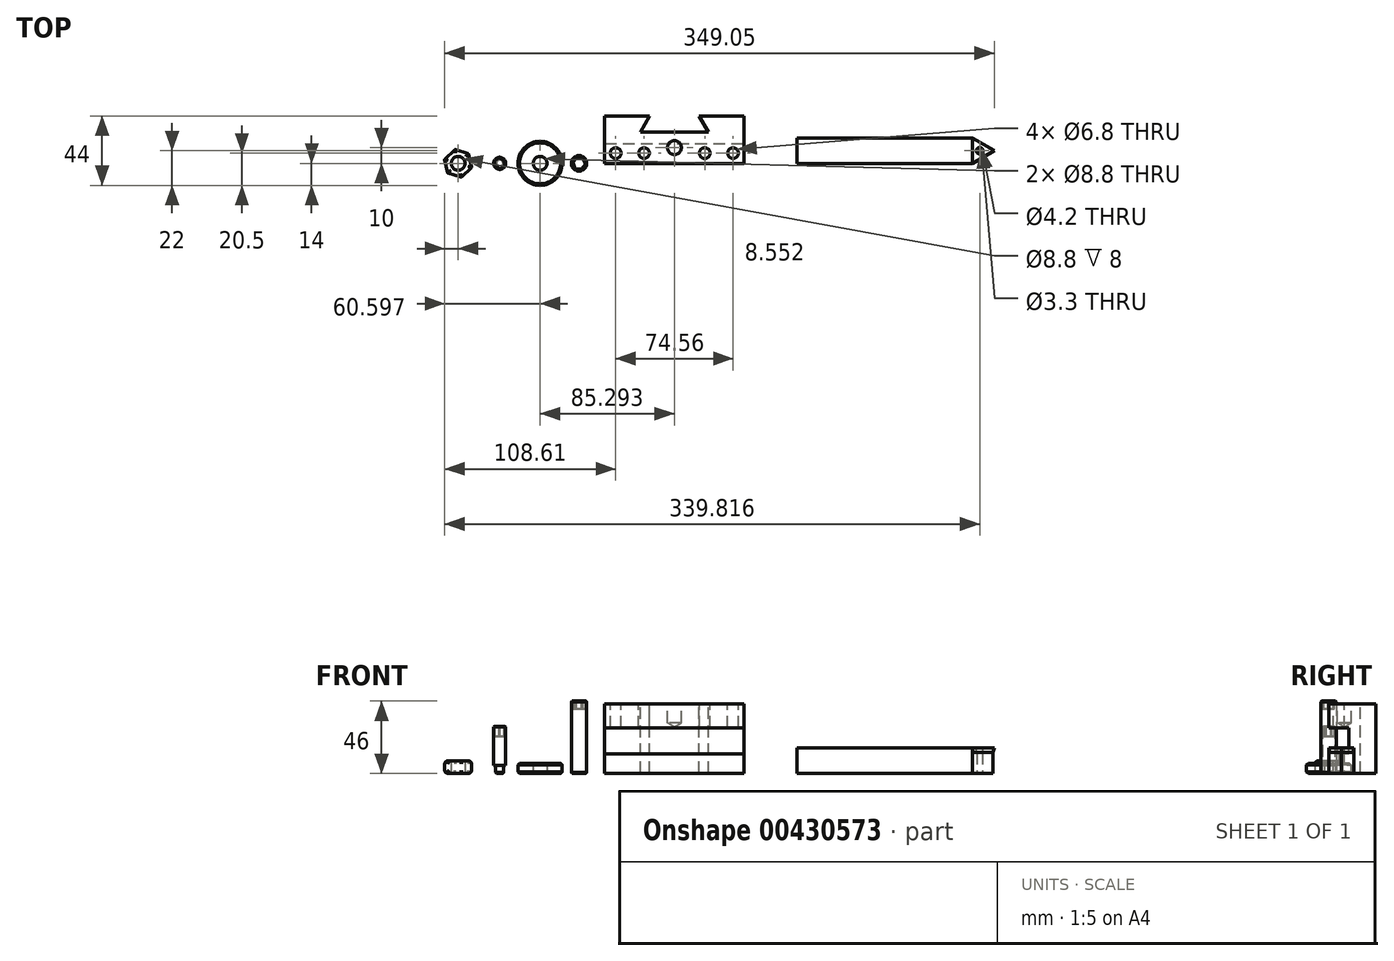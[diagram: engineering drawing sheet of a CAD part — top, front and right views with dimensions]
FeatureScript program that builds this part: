
annotation { "Feature Type Name" : "Feature", "Feature Type Description" : "" }
export const myFeature = defineFeature(function(context is Context, id is Id, definition is map)
    precondition{}
    {
        {
            var Q0;
            Q0=qCreatedBy(makeId("Front.planeOp"),FACE);
            var sketch = newSketch(context, id + "F0", { "sketchPlane" : qUnion([Q0])});
            skLineSegment(sketch, "E0.bottom", {"start": v(0, 0) * mm, "end": v(88.56, 0) * mm});
            skLineSegment(sketch, "E0.top", {"start": v(0, 44.12) * mm, "end": v(88.56, 44.12) * mm});
            skLineSegment(sketch, "E0.left", {"start": v(0, 0) * mm, "end": v(0, 44.12) * mm});
            skLineSegment(sketch, "E0.right", {"start": v(88.56, 0) * mm, "end": v(88.56, 44.12) * mm});
            skLineSegment(sketch, "E1", {"start": v(0, 12.4) * mm, "end": v(88.56, 12.4) * mm});
            skLineSegment(sketch, "E2", {"start": v(0, 28.9) * mm, "end": v(88.56, 28.9) * mm});
            skSolve(sketch);
        }
        {
            var Q0;
            Q0=qSketchRegion(id+"F0",true);
            extrude(context, id + "F1", {"entities" : qUnion([Q0]), "oppositeDirection" : true, "depth" : 30 * mm});
        }
        {
            var Q0;
            {var subQ0=sQuery(id+"F0.wireOp",EDGE,"E1");Q0=makeQuery(id+"F0.imprint","IMPRINT",FACE,{"disambiguationData":[TD([[makeQuery(id+"F0.imprint","IMPRINT",EDGE,{"derivedFrom":subQ0}),1.0]])]});}
            extrude(context, id + "F2", {"entities" : qUnion([Q0]), "operationType" : NewBodyOperationType.REMOVE, "oppositeDirection" : true, "depth" : 12.7 * mm});
        }
        {
            var Q0;
            Q0=makeQuery(id+"F1.opExtrude","SWEPT_FACE",FACE,{"disambiguationData":[OSD([sQuery(id+"F0.wireOp",EDGE,"E0.top")])]});
            var sketch = newSketch(context, id + "F3", { "sketchPlane" : qUnion([Q0])});
            skLineSegment(sketch, "E3", {"start": v(0, 6.5) * mm, "end": v(88.56, 6.5) * mm, "construction": true});
            skPoint(sketch, "E4", {"position": v(7, 6.5) * mm});
            skPoint(sketch, "E5", {"position": v(25, 6.5) * mm});
            skPoint(sketch, "E6", {"position": v(81.56, 6.5) * mm});
            skPoint(sketch, "E7", {"position": v(63.56, 6.5) * mm});
            skLineSegment(sketch, "E8", {"start": v(22.78, 20) * mm, "end": v(65.78, 20) * mm});
            skLineSegment(sketch, "E9", {"start": v(44.28, 17.17) * mm, "end": v(44.28, 26.13) * mm, "construction": true});
            skPoint(sketch, "E9.startSnap0", {"position": v(44.28, 30) * mm});
            skLineSegment(sketch, "E10", {"start": v(65.78, 20) * mm, "end": v(60, 30) * mm});
            skLineSegment(sketch, "E11", {"start": v(22.78, 20) * mm, "end": v(28.55, 30) * mm});
            skLineSegment(sketch, "E12", {"start": v(36.04, 10) * mm, "end": v(51.79, 10) * mm, "construction": true});
            skPoint(sketch, "E13", {"position": v(44.28, 10) * mm});
            skSolve(sketch);
        }
        {
            var Q0;
            Q0=qSketchRegion(id+"F3",true);
            var Q1;
            Q1=makeQuery(id+"F3.imprint","IMPRINT",FACE,{"disambiguationData":[TD([[makeQuery(id+"F3.imprint","IMPRINT",EDGE,{"derivedFrom":sQuery(id+"F3.wireOp",EDGE,"E8")}),1.0]])]});
            extrude(context, id + "F4", {"entities" : qUnion([Q0, Q1]), "operationType" : NewBodyOperationType.REMOVE, "endBound" : BoundingType.UP_TO_NEXT, "oppositeDirection" : true, "depth" : 25 * mm});
        }
        {
            var Q0;
            Q0=sQuery(id+"F3.wireOp",VERTEX,"E4");
            var Q1;
            Q1=sQuery(id+"F3.wireOp",VERTEX,"E5");
            var Q2;
            Q2=sQuery(id+"F3.wireOp",VERTEX,"E7");
            var Q3;
            Q3=sQuery(id+"F3.wireOp",VERTEX,"E6");
            var Q4;
            Q4=makeQuery(id+"F1.opExtrude","SWEPT_BODY",BODY,{"disambiguationData":[OSD([sQuery(id+"F0.wireOp",EDGE,"E0.bottom"),sQuery(id+"F0.wireOp",EDGE,"E0.top"),sQuery(id+"F0.wireOp",EDGE,"E0.left"),sQuery(id+"F0.wireOp",EDGE,"E0.right")])]});
            hole(context, id + "F5", {"style" : HoleStyle.SIMPLE, "endStyle" : HoleEndStyle.BLIND, "standardTappedOrClearance" : lookupTablePath({ "standard" : "ISO", "engagement" : "75%", "pitch" : "1.25 mm", "size" : "M8", "type" : "Tapped" }), "standardBlindInLast" : lookupTablePath({ "standard" : "ISO", "engagement" : "75%", "pitch" : "1.25 mm", "size" : "M8", "type" : "Tapped" }), "holeDiameter" : 6.8 * mm, "showTappedDepth" : true, "holeDepth" : 15.75 * mm, "isTappedThrough" : true, "tappedDepth" : 12 * mm, "tapClearance" : 3, "startFromSketch" : true, "locations" : qUnion([Q0, Q1, Q2, Q3]), "scope" : qUnion([Q4]), "majorDiameter" : 8 * mm});
        }
        {
            var Q0;
            Q0=sQuery(id+"F3.wireOp",VERTEX,"E13");
            var Q1;
            Q1=makeQuery(id+"F1.opExtrude","SWEPT_BODY",BODY,{"disambiguationData":[OSD([sQuery(id+"F0.wireOp",EDGE,"E0.bottom"),sQuery(id+"F0.wireOp",EDGE,"E0.top"),sQuery(id+"F0.wireOp",EDGE,"E0.left"),sQuery(id+"F0.wireOp",EDGE,"E0.right")])]});
            hole(context, id + "F6", {"style" : HoleStyle.SIMPLE, "endStyle" : HoleEndStyle.BLIND, "standardTappedOrClearance" : lookupTablePath({ "standard" : "ISO", "engagement" : "75%", "pitch" : "1.25 mm", "size" : "M10", "type" : "Tapped" }), "standardBlindInLast" : lookupTablePath({ "standard" : "ISO", "engagement" : "75%", "pitch" : "1.25 mm", "size" : "M10", "type" : "Tapped" }), "holeDiameter" : 8.8 * mm, "showTappedDepth" : true, "holeDepth" : 12 * mm, "isTappedThrough" : true, "tappedDepth" : 8.25 * mm, "tapClearance" : 3, "startFromSketch" : true, "locations" : qUnion([Q0]), "scope" : qUnion([Q1]), "majorDiameter" : 10 * mm});
        }
        {
            var Q0;
            Q0=qCreatedBy(makeId("Top.planeOp"),FACE);
            var sketch = newSketch(context, id + "F7", { "sketchPlane" : qUnion([Q0])});
            skCircle(sketch, "E14", {"center": v(-16.29, 0) * mm, "radius": 4.9 * mm});
            skSolve(sketch);
        }
        {
            var Q0;
            Q0=qSketchRegion(id+"F7",true);
            extrude(context, id + "F8", {"entities" : qUnion([Q0]), "depth" : 46 * mm});
        }
        {
            var Q0;
            Q0=makeQuery(id+"F8.opExtrude","CAP_EDGE",EDGE,{"disambiguationData":[OSD([sQuery(id+"F7.wireOp",EDGE,"E14")])],"isStart":false});
            var Q1;
            Q1=makeQuery(id+"F8.opExtrude","CAP_EDGE",EDGE,{"disambiguationData":[OSD([sQuery(id+"F7.wireOp",EDGE,"E14")])],"isStart":true});
            chamfer(context, id + "F9", {"entities" : qUnion([Q0, Q1]), "width" : .5 * mm, "tangentPropagation" : true});
        }
        {
            var Q0;
            Q0=makeQuery(id+"F8.opExtrude","CAP_FACE",FACE,{"disambiguationData":[OSD([sQuery(id+"F7.wireOp",EDGE,"E14")])],"isStart":false});
            var sketch = newSketch(context, id + "F10", { "sketchPlane" : qUnion([Q0])});
            skCircle(sketch, "E15.cCircle", {"center": v(-16.29, 0) * mm, "radius": 4 * mm, "construction": true});
            skLineSegment(sketch, "E15.0", {"start": v(-13.87, 3.19) * mm, "end": v(-12.32, -0.5) * mm});
            skLineSegment(sketch, "E15.1", {"start": v(-12.32, -0.5) * mm, "end": v(-14.73, -3.69) * mm});
            skLineSegment(sketch, "E15.2", {"start": v(-14.73, -3.69) * mm, "end": v(-18.7, -3.19) * mm});
            skLineSegment(sketch, "E15.3", {"start": v(-18.7, -3.19) * mm, "end": v(-20.26, 0.5) * mm});
            skLineSegment(sketch, "E15.4", {"start": v(-20.26, 0.5) * mm, "end": v(-17.84, 3.69) * mm});
            skLineSegment(sketch, "E15.5", {"start": v(-17.84, 3.69) * mm, "end": v(-13.87, 3.19) * mm});
            skSolve(sketch);
        }
        {
            var Q0;
            Q0=makeQuery(id+"F10.imprint","IMPRINT",FACE,{"disambiguationData":[TD([[makeQuery(id+"F10.imprint","IMPRINT",EDGE,{"derivedFrom":sQuery(id+"F10.wireOp",EDGE,"E15.0")}),-1.0]])]});
            extrude(context, id + "F11", {"entities" : qUnion([Q0]), "operationType" : NewBodyOperationType.REMOVE, "oppositeDirection" : true, "depth" : 5 * mm});
        }
        {
            var Q0;
            Q0=qCreatedBy(makeId("Top.planeOp"),FACE);
            var sketch = newSketch(context, id + "F12", { "sketchPlane" : qUnion([Q0])});
            skCircle(sketch, "E16", {"center": v(-41.01, 0) * mm, "radius": 14 * mm});
            skSolve(sketch);
        }
        {
            var Q0;
            Q0=makeQuery(id+"F12.imprint","IMPRINT",FACE,{"disambiguationData":[TD([[makeQuery(id+"F12.imprint","IMPRINT",EDGE,{"derivedFrom":sQuery(id+"F12.wireOp",EDGE,"E16")}),1.0]])]});
            extrude(context, id + "F13", {"entities" : qUnion([Q0]), "depth" : 6.43 * mm});
        }
        {
            var Q0;
            Q0=makeQuery(id+"F13.opExtrude","CAP_EDGE",EDGE,{"disambiguationData":[OSD([sQuery(id+"F12.wireOp",EDGE,"E16")])],"isStart":false});
            var Q1;
            Q1=makeQuery(id+"F13.opExtrude","CAP_EDGE",EDGE,{"disambiguationData":[OSD([sQuery(id+"F12.wireOp",EDGE,"E16")])],"isStart":true});
            chamfer(context, id + "F14", {"entities" : qUnion([Q0, Q1]), "width" : 1 * mm, "tangentPropagation" : true});
        }
        {
            var Q0;
            Q0=sQuery(id+"F12.wireOp",VERTEX,"E16.center");
            var Q1;
            Q1=makeQuery(id+"F13.opExtrude","SWEPT_BODY",BODY,{"disambiguationData":[OSD([sQuery(id+"F12.wireOp",EDGE,"E16")])]});
            hole(context, id + "F15", {"style" : HoleStyle.SIMPLE, "endStyle" : HoleEndStyle.THROUGH, "oppositeDirection" : true, "standardTappedOrClearance" : lookupTablePath({ "standard" : "ISO", "engagement" : "75%", "pitch" : "1.25 mm", "size" : "M10", "type" : "Tapped" }), "standardBlindInLast" : lookupTablePath({ "standard" : "ISO", "engagement" : "75%", "pitch" : "1.25 mm", "size" : "M10", "type" : "Tapped" }), "holeDiameter" : 8.8 * mm, "showTappedDepth" : true, "isTappedThrough" : true, "tappedDepth" : 12 * mm, "tapClearance" : 3, "startFromSketch" : true, "locations" : qUnion([Q0]), "scope" : qUnion([Q1]), "majorDiameter" : 10 * mm});
        }
        {
            var Q0;
            Q0=qCreatedBy(makeId("Top.planeOp"),FACE);
            var sketch = newSketch(context, id + "F16", { "sketchPlane" : qUnion([Q0])});
            skCircle(sketch, "E17", {"center": v(-66.7, 0) * mm, "radius": 2.6 * mm});
            skSolve(sketch);
        }
        {
            var Q0;
            Q0=qSketchRegion(id+"F16",true);
            extrude(context, id + "F17", {"entities" : qUnion([Q0]), "depth" : 5 * mm});
        }
        {
            var Q0;
            Q0=makeQuery(id+"F17.opExtrude","CAP_FACE",FACE,{"disambiguationData":[OSD([sQuery(id+"F16.wireOp",EDGE,"E17")])],"isStart":false});
            var sketch = newSketch(context, id + "F18", { "sketchPlane" : qUnion([Q0])});
            skCircle(sketch, "E18", {"center": v(-66.7, 0) * mm, "radius": 3.85 * mm});
            skSolve(sketch);
        }
        {
            var Q0;
            Q0=qSketchRegion(id+"F18",true);
            extrude(context, id + "F19", {"entities" : qUnion([Q0]), "operationType" : NewBodyOperationType.ADD, "depth" : 25 * mm});
        }
        {
            var Q0;
            Q0=makeQuery(id+"F19.opExtrude","CAP_FACE",FACE,{"disambiguationData":[OSD([sQuery(id+"F18.wireOp",EDGE,"E18")])],"isStart":false});
            var sketch = newSketch(context, id + "F20", { "sketchPlane" : qUnion([Q0])});
            skCircle(sketch, "E19.cCircle", {"center": v(-66.7, 0) * mm, "radius": 3.03 * mm, "construction": true});
            skLineSegment(sketch, "E19.0", {"start": v(-67, 3.49) * mm, "end": v(-63.82, 2) * mm});
            skLineSegment(sketch, "E19.1", {"start": v(-63.82, 2) * mm, "end": v(-63.52, -1.48) * mm});
            skLineSegment(sketch, "E19.2", {"start": v(-63.52, -1.48) * mm, "end": v(-66.39, -3.49) * mm});
            skLineSegment(sketch, "E19.3", {"start": v(-66.39, -3.49) * mm, "end": v(-69.56, -2) * mm});
            skLineSegment(sketch, "E19.4", {"start": v(-69.56, -2) * mm, "end": v(-69.86, 1.48) * mm});
            skLineSegment(sketch, "E19.5", {"start": v(-69.86, 1.48) * mm, "end": v(-67, 3.49) * mm});
            skPoint(sketch, "E19.0.midPoint", {"position": v(-65.41, 2.75) * mm});
            skSolve(sketch);
        }
        {
            var Q0;
            Q0=makeQuery(id+"F20.imprint","IMPRINT",FACE,{"disambiguationData":[TD([[makeQuery(id+"F20.imprint","IMPRINT",EDGE,{"derivedFrom":sQuery(id+"F20.wireOp",EDGE,"E19.0")}),-1.0]])]});
            extrude(context, id + "F21", {"entities" : qUnion([Q0]), "operationType" : NewBodyOperationType.REMOVE, "oppositeDirection" : true, "depth" : 6.4 * mm});
        }
        {
            var Q0;
            Q0=qCreatedBy(makeId("Top.planeOp"),FACE);
            var sketch = newSketch(context, id + "F22", { "sketchPlane" : qUnion([Q0])});
            skCircle(sketch, "E20.cCircle", {"center": v(-93.06, 0) * mm, "radius": 9 * mm, "construction": true});
            skLineSegment(sketch, "E20.0", {"start": v(-86.48, 6.14) * mm, "end": v(-84.45, -2.63) * mm});
            skLineSegment(sketch, "E20.1", {"start": v(-84.45, -2.63) * mm, "end": v(-91.03, -8.77) * mm});
            skLineSegment(sketch, "E20.2", {"start": v(-91.03, -8.77) * mm, "end": v(-99.64, -6.14) * mm});
            skLineSegment(sketch, "E20.3", {"start": v(-99.64, -6.14) * mm, "end": v(-101.67, 2.63) * mm});
            skLineSegment(sketch, "E20.4", {"start": v(-101.67, 2.63) * mm, "end": v(-95.09, 8.77) * mm});
            skLineSegment(sketch, "E20.5", {"start": v(-95.09, 8.77) * mm, "end": v(-86.48, 6.14) * mm});
            skSolve(sketch);
        }
        {
            var Q0;
            Q0=makeQuery(id+"F22.imprint","IMPRINT",FACE,{"disambiguationData":[TD([[makeQuery(id+"F22.imprint","IMPRINT",EDGE,{"derivedFrom":sQuery(id+"F22.wireOp",EDGE,"E20.0")}),-1.0]])]});
            extrude(context, id + "F23", {"entities" : qUnion([Q0]), "depth" : 8 * mm});
        }
        {
            var Q0;
            Q0=sQuery(id+"F22.wireOp",VERTEX,"E20.cCircle.center");
            var Q1;
            Q1=makeQuery(id+"F23.opExtrude","SWEPT_BODY",BODY,{"disambiguationData":[OSD([sQuery(id+"F22.wireOp",EDGE,"E20.0"),sQuery(id+"F22.wireOp",EDGE,"E20.1"),sQuery(id+"F22.wireOp",EDGE,"E20.2"),sQuery(id+"F22.wireOp",EDGE,"E20.3"),sQuery(id+"F22.wireOp",EDGE,"E20.4"),sQuery(id+"F22.wireOp",EDGE,"E20.5")])]});
            hole(context, id + "F24", {"style" : HoleStyle.SIMPLE, "endStyle" : HoleEndStyle.THROUGH, "oppositeDirection" : true, "standardTappedOrClearance" : lookupTablePath({ "standard" : "ISO", "engagement" : "75%", "pitch" : "1.25 mm", "size" : "M10", "type" : "Tapped" }), "standardBlindInLast" : lookupTablePath({ "standard" : "ISO", "engagement" : "75%", "pitch" : "1.25 mm", "size" : "M10", "type" : "Tapped" }), "holeDiameter" : 8.8 * mm, "showTappedDepth" : true, "isTappedThrough" : true, "tappedDepth" : 12 * mm, "tapClearance" : 3, "startFromSketch" : true, "locations" : qUnion([Q0]), "scope" : qUnion([Q1]), "majorDiameter" : 10 * mm});
        }
        {
            var Q0;
            Q0=makeQuery(id+"F23.opExtrude","CAP_EDGE",EDGE,{"disambiguationData":[OSD([sQuery(id+"F22.wireOp",EDGE,"E20.4")])],"isStart":false});
            var Q1;
            Q1=makeQuery(id+"F23.opExtrude","CAP_EDGE",EDGE,{"disambiguationData":[OSD([sQuery(id+"F22.wireOp",EDGE,"E20.5")])],"isStart":false});
            var Q2;
            Q2=makeQuery(id+"F23.opExtrude","CAP_EDGE",EDGE,{"disambiguationData":[OSD([sQuery(id+"F22.wireOp",EDGE,"E20.0")])],"isStart":false});
            var Q3;
            Q3=makeQuery(id+"F23.opExtrude","CAP_EDGE",EDGE,{"disambiguationData":[OSD([sQuery(id+"F22.wireOp",EDGE,"E20.1")])],"isStart":false});
            var Q4;
            Q4=makeQuery(id+"F23.opExtrude","CAP_EDGE",EDGE,{"disambiguationData":[OSD([sQuery(id+"F22.wireOp",EDGE,"E20.2")])],"isStart":false});
            var Q5;
            Q5=makeQuery(id+"F23.opExtrude","CAP_EDGE",EDGE,{"disambiguationData":[OSD([sQuery(id+"F22.wireOp",EDGE,"E20.3")])],"isStart":false});
            var Q6;
            Q6=makeQuery(id+"F23.opExtrude","CAP_EDGE",EDGE,{"disambiguationData":[OSD([sQuery(id+"F22.wireOp",EDGE,"E20.3")])],"isStart":true});
            var Q7;
            Q7=makeQuery(id+"F23.opExtrude","CAP_EDGE",EDGE,{"disambiguationData":[OSD([sQuery(id+"F22.wireOp",EDGE,"E20.4")])],"isStart":true});
            var Q8;
            Q8=makeQuery(id+"F23.opExtrude","CAP_EDGE",EDGE,{"disambiguationData":[OSD([sQuery(id+"F22.wireOp",EDGE,"E20.5")])],"isStart":true});
            var Q9;
            Q9=makeQuery(id+"F23.opExtrude","CAP_EDGE",EDGE,{"disambiguationData":[OSD([sQuery(id+"F22.wireOp",EDGE,"E20.0")])],"isStart":true});
            var Q10;
            Q10=makeQuery(id+"F23.opExtrude","CAP_EDGE",EDGE,{"disambiguationData":[OSD([sQuery(id+"F22.wireOp",EDGE,"E20.1")])],"isStart":true});
            var Q11;
            Q11=makeQuery(id+"F23.opExtrude","CAP_EDGE",EDGE,{"disambiguationData":[OSD([sQuery(id+"F22.wireOp",EDGE,"E20.2")])],"isStart":true});
            fillet(context, id + "F25", {"entities" : qUnion([Q0, Q1, Q2, Q3, Q4, Q5, Q6, Q7, Q8, Q9, Q10, Q11]), "radius" : 2 * mm, "tangentPropagation" : true, "allowEdgeOverflow" : false});
        }
        {
            var Q0;
            Q0=makeQuery(id+"F23.opExtrude","SWEPT_EDGE",EDGE,{"disambiguationData":[OSD([sQuery(id+"F22.wireOp",EDGE,"E20.2"),sQuery(id+"F22.wireOp",EDGE,"E20.3")])]});
            var Q1;
            Q1=makeQuery(id+"F23.opExtrude","SWEPT_EDGE",EDGE,{"disambiguationData":[OSD([sQuery(id+"F22.wireOp",EDGE,"E20.1"),sQuery(id+"F22.wireOp",EDGE,"E20.2")])]});
            var Q2;
            Q2=makeQuery(id+"F23.opExtrude","SWEPT_EDGE",EDGE,{"disambiguationData":[OSD([sQuery(id+"F22.wireOp",EDGE,"E20.0"),sQuery(id+"F22.wireOp",EDGE,"E20.1")])]});
            var Q3;
            Q3=makeQuery(id+"F23.opExtrude","SWEPT_EDGE",EDGE,{"disambiguationData":[OSD([sQuery(id+"F22.wireOp",EDGE,"E20.3"),sQuery(id+"F22.wireOp",EDGE,"E20.4")])]});
            var Q4;
            Q4=makeQuery(id+"F23.opExtrude","SWEPT_EDGE",EDGE,{"disambiguationData":[OSD([sQuery(id+"F22.wireOp",EDGE,"E20.4"),sQuery(id+"F22.wireOp",EDGE,"E20.5")])]});
            var Q5;
            Q5=makeQuery(id+"F23.opExtrude","SWEPT_EDGE",EDGE,{"disambiguationData":[OSD([sQuery(id+"F22.wireOp",EDGE,"E20.0"),sQuery(id+"F22.wireOp",EDGE,"E20.5")])]});
            fillet(context, id + "F26", {"entities" : qUnion([Q0, Q1, Q2, Q3, Q4, Q5]), "radius" : .5 * mm, "tangentPropagation" : true, "allowEdgeOverflow" : false});
        }
        {
            var Q0;
            Q0=qCreatedBy(makeId("Front.planeOp"),FACE);
            var sketch = newSketch(context, id + "F27", { "sketchPlane" : qUnion([Q0])});
            skLineSegment(sketch, "E21.bottom", {"start": v(122.09, 0) * mm, "end": v(245.45, 0) * mm});
            skLineSegment(sketch, "E21.top", {"start": v(122.09, 16.3) * mm, "end": v(233.59, 16.3) * mm});
            skLineSegment(sketch, "E21.left", {"start": v(122.09, 0) * mm, "end": v(122.09, 16.3) * mm});
            skLineSegment(sketch, "E22", {"start": v(233.59, 16.3) * mm, "end": v(233.59, 13.3) * mm});
            skLineSegment(sketch, "E23", {"start": v(233.59, 13.3) * mm, "end": v(246.59, 13.3) * mm});
            skLineSegment(sketch, "E24", {"start": v(246.59, 13.3) * mm, "end": v(246.59, 0) * mm});
            skLineSegment(sketch, "E25", {"start": v(246.59, 0) * mm, "end": v(245.45, 0) * mm});
            skSolve(sketch);
        }
        {
            var Q0;
            Q0=makeQuery(id+"F27.imprint","IMPRINT",FACE,{"disambiguationData":[TD([[makeQuery(id+"F27.imprint","IMPRINT",EDGE,{"derivedFrom":sQuery(id+"F27.wireOp",EDGE,"E21.bottom")}),1.0]])]});
            extrude(context, id + "F28", {"entities" : qUnion([Q0]), "oppositeDirection" : true, "depth" : 16 * mm});
        }
        {
            var Q0;
            Q0=makeQuery(id+"F28.opExtrude","SWEPT_FACE",FACE,{"disambiguationData":[OSD([sQuery(id+"F27.wireOp",EDGE,"E23")])]});
            var sketch = newSketch(context, id + "F29", { "sketchPlane" : qUnion([Q0])});
            skLineSegment(sketch, "E26", {"start": v(233.59, 16) * mm, "end": v(246.59, 8) * mm});
            skLineSegment(sketch, "E27", {"start": v(246.59, 8) * mm, "end": v(233.59, 0) * mm});
            skSolve(sketch);
        }
        {
            var Q0;
            {var subQ0=sQuery(id+"F29.wireOp",EDGE,"E26");Q0=makeQuery(id+"F29.imprint","IMPRINT",FACE,{"disambiguationData":[TD([[makeQuery(id+"F29.imprint","IMPRINT",EDGE,{"derivedFrom":subQ0}),1.0]])]});}
            var Q1;
            {var subQ0=sQuery(id+"F29.wireOp",EDGE,"E27");Q1=makeQuery(id+"F29.imprint","IMPRINT",FACE,{"disambiguationData":[TD([[makeQuery(id+"F29.imprint","IMPRINT",EDGE,{"derivedFrom":subQ0}),1.0]])]});}
            extrude(context, id + "F30", {"entities" : qUnion([Q0, Q1]), "operationType" : NewBodyOperationType.REMOVE, "endBound" : BoundingType.UP_TO_NEXT, "oppositeDirection" : true, "depth" : 25 * mm});
        }
        {
            var Q0;
            Q0=makeQuery(id+"F28.opExtrude","SWEPT_FACE",FACE,{"disambiguationData":[OSD([sQuery(id+"F27.wireOp",EDGE,"E21.top")])]});
            var sketch = newSketch(context, id + "F31", { "sketchPlane" : qUnion([Q0])});
            skLineSegment(sketch, "E28", {"start": v(233.59, 0) * mm, "end": v(247.44, 8) * mm});
            skLineSegment(sketch, "E29", {"start": v(247.44, 8) * mm, "end": v(233.59, 16) * mm});
            skLineSegment(sketch, "E30", {"start": v(233.59, 16) * mm, "end": v(233.59, 0) * mm});
            skLineSegment(sketch, "E31", {"start": v(247.44, 8) * mm, "end": v(233.59, 8) * mm, "construction": true});
            skLineSegment(sketch, "E32", {"start": v(233.59, 0) * mm, "end": v(240.52, 12) * mm, "construction": true});
            skPoint(sketch, "E33", {"position": v(238.2, 8) * mm});
            skSolve(sketch);
        }
        {
            var Q0;
            Q0=qSketchRegion(id+"F31",true);
            extrude(context, id + "F32", {"entities" : qUnion([Q0]), "oppositeDirection" : true, "depth" : 3 * mm, "hasDraft" : true, "draftAngle" : 7 * degree, "draftPullDirection" : true});
        }
        {
            var Q0;
            Q0=sQuery(id+"F31.wireOp",VERTEX,"E33");
            var Q1;
            Q1=makeQuery(id+"F32.opExtrude","SWEPT_BODY",BODY,{"disambiguationData":[OSD([sQuery(id+"F31.wireOp",EDGE,"E28"),sQuery(id+"F31.wireOp",EDGE,"E29"),sQuery(id+"F31.wireOp",EDGE,"E30")])]});
            hole(context, id + "F33", {"style" : HoleStyle.SIMPLE, "endStyle" : HoleEndStyle.BLIND, "standardTappedOrClearance" : lookupTablePath({ "standard" : "ISO", "fit" : "Close", "size" : "M4", "type" : "Clearance" }), "standardBlindInLast" : lookupTablePath({ "fit" : "Close", "standard" : "ISO", "size" : "M4", "type" : "Clearance" }), "holeDiameter" : 4.2 * mm, "holeDepth" : 3 * mm, "isTappedThrough" : true, "tappedDepth" : 12 * mm, "tapClearance" : 3, "startFromSketch" : true, "locations" : qUnion([Q0]), "scope" : qUnion([Q1])});
        }
        {
            var Q0;
            Q0=makeQuery(id+"F28.opExtrude","SWEPT_FACE",FACE,{"disambiguationData":[OSD([sQuery(id+"F27.wireOp",EDGE,"E21.bottom"),sQuery(id+"F27.wireOp",EDGE,"E25")])]});
            var sketch = newSketch(context, id + "F34", { "sketchPlane" : qUnion([Q0])});
            skPoint(sketch, "E34", {"position": v(238.2, -8) * mm});
            skSolve(sketch);
        }
        {
            var Q0;
            Q0=sQuery(id+"F34.wireOp",VERTEX,"E34");
            var Q1;
            Q1=makeQuery(id+"F28.opExtrude","SWEPT_BODY",BODY,{"disambiguationData":[OSD([sQuery(id+"F27.wireOp",EDGE,"E21.bottom"),sQuery(id+"F27.wireOp",EDGE,"E21.top"),sQuery(id+"F27.wireOp",EDGE,"E21.left"),sQuery(id+"F27.wireOp",EDGE,"E22"),sQuery(id+"F27.wireOp",EDGE,"E23"),sQuery(id+"F27.wireOp",EDGE,"E24"),sQuery(id+"F27.wireOp",EDGE,"E25")])]});
            hole(context, id + "F35", {"style" : HoleStyle.SIMPLE, "endStyle" : HoleEndStyle.THROUGH, "standardTappedOrClearance" : lookupTablePath({ "standard" : "ISO", "engagement" : "75%", "pitch" : "0.7 mm", "size" : "M4", "type" : "Tapped" }), "standardBlindInLast" : lookupTablePath({ "standard" : "ISO", "engagement" : "75%", "pitch" : "0.7 mm", "size" : "M4", "type" : "Tapped" }), "holeDiameter" : 3.3 * mm, "showTappedDepth" : true, "isTappedThrough" : true, "tappedDepth" : 12 * mm, "tapClearance" : 3, "startFromSketch" : true, "locations" : qUnion([Q0]), "scope" : qUnion([Q1]), "majorDiameter" : 4 * mm});
        }
        {
            var Q0;
            Q0=makeQuery(id+"F19.opExtrude","CAP_EDGE",EDGE,{"disambiguationData":[OSD([sQuery(id+"F18.wireOp",EDGE,"E18")])],"isStart":false});
            var Q1;
            Q1=makeQuery(id+"F17.opExtrude","CAP_EDGE",EDGE,{"disambiguationData":[OSD([sQuery(id+"F16.wireOp",EDGE,"E17")])],"isStart":true});
            chamfer(context, id + "F36", {"entities" : qUnion([Q0, Q1]), "width" : .5 * mm, "tangentPropagation" : true});
        }
    });
